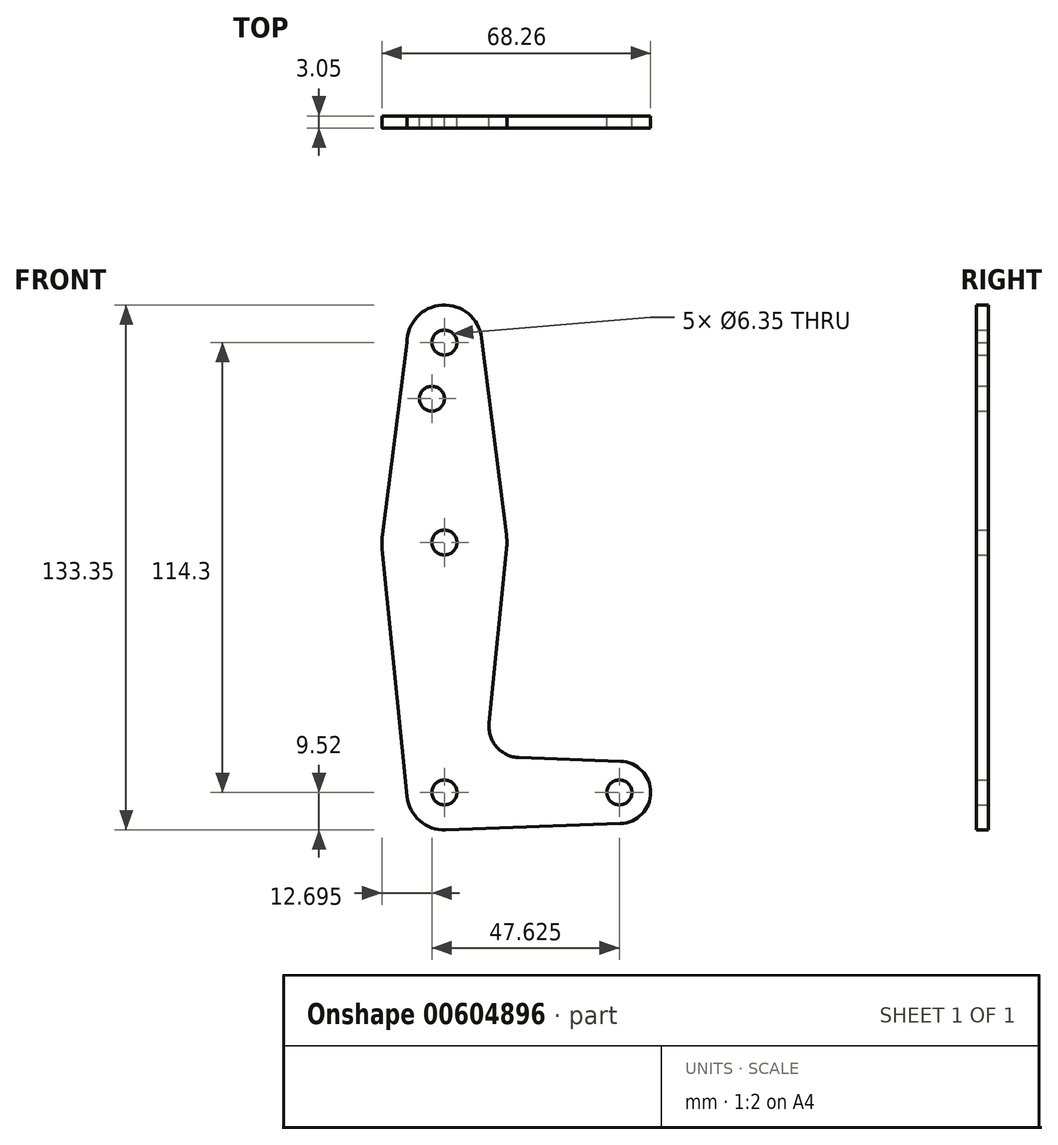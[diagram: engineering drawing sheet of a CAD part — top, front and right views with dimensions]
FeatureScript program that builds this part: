
annotation { "Feature Type Name" : "Feature", "Feature Type Description" : "" }
export const myFeature = defineFeature(function(context is Context, id is Id, definition is map)
    precondition{}
    {
        {
            var Q0;
            Q0=qCreatedBy(makeId("Front.planeOp"),FACE);
            var sketch = newSketch(context, id + "F0", { "sketchPlane" : qUnion([Q0])});
            skCircle(sketch, "E0", {"center": v(0, 0) * mm, "radius": 9.53 * mm});
            skLineSegment(sketch, "E1", {"start": v(0, 0) * mm, "end": v(0, 114.3) * mm, "construction": true});
            skCircle(sketch, "E2", {"center": v(0, 114.3) * mm, "radius": 9.53 * mm});
            skCircle(sketch, "E3", {"center": v(0, 63.5) * mm, "radius": 15.88 * mm});
            skLineSegment(sketch, "E4", {"start": v(0, 0) * mm, "end": v(44.45, 0) * mm, "construction": true});
            skCircle(sketch, "E5", {"center": v(44.45, 0) * mm, "radius": 7.94 * mm});
            skLineSegment(sketch, "E6", {"start": v(-9.53, 114.3) * mm, "end": v(-15.75, 65.5) * mm});
            skLineSegment(sketch, "E7", {"start": v(9.45, 115.5) * mm, "end": v(15.75, 65.48) * mm});
            skLineSegment(sketch, "E8", {"start": v(-9.48, -0.95) * mm, "end": v(-15.8, 61.91) * mm});
            skCircle(sketch, "E9", {"center": v(0, 114.3) * mm, "radius": 3.18 * mm});
            skCircle(sketch, "E10", {"center": v(0, 63.5) * mm, "radius": 3.18 * mm});
            skCircle(sketch, "E11", {"center": v(0, 0) * mm, "radius": 3.18 * mm});
            skCircle(sketch, "E12", {"center": v(44.45, 0) * mm, "radius": 3.18 * mm});
            skCircle(sketch, "E13", {"center": v(-3.18, 100.03) * mm, "radius": 3.18 * mm});
            skLineSegment(sketch, "E14", {"start": v(44.73, -7.93) * mm, "end": v(0.34, -9.52) * mm});
            skLineSegment(sketch, "E15", {"start": v(15.8, 61.91) * mm, "end": v(11.34, 17.6) * mm});
            skLineSegment(sketch, "E16", {"start": v(44.73, 7.93) * mm, "end": v(18.97, 8.85) * mm});
            skArc(sketch, "E17.filletArc", {"start": v(11.34, 17.6) * mm, "mid": v(13.26, 11.57) * mm, "end": v(18.97, 8.85) * mm});
            skSolve(sketch);
        }
        {
            var Q0;
            Q0 = qSketchRegion(id + "F0", true);
            extrude(context, id + "F1", {"entities" : qUnion([Q0]), "depth" : 3.05 * mm, "offsetDistance" : 25.4 * mm});
        }
    });
